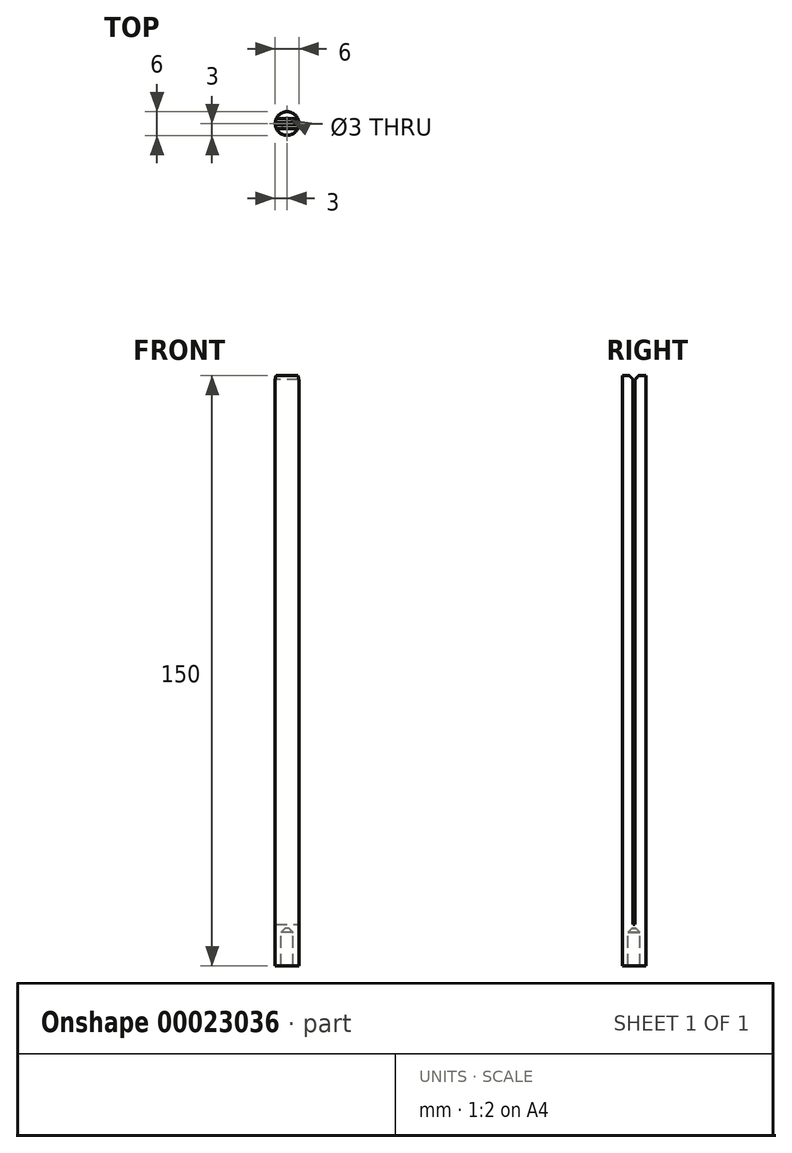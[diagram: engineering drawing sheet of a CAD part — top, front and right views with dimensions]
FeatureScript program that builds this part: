
annotation { "Feature Type Name" : "Feature", "Feature Type Description" : "" }
export const myFeature = defineFeature(function(context is Context, id is Id, definition is map)
    precondition{}
    {
        {
            var Q0;
            Q0=qCreatedBy(makeId("Top.planeOp"),FACE);
            var sketch = newSketch(context, id + "F0", { "sketchPlane" : qUnion([Q0])});
            skCircle(sketch, "E0", {"center": v(0, 0) * mm, "radius": 1.5 * mm});
            skCircle(sketch, "E1", {"center": v(0, 0) * mm, "radius": 3 * mm});
            skLineSegment(sketch, "E2", {"start": v(-3, 0) * mm, "end": v(3, 0) * mm, "construction": true});
            skLineSegment(sketch, "E3", {"start": v(-2.99, 0.25) * mm, "end": v(2.99, 0.25) * mm});
            skLineSegment(sketch, "E4.MirrorCS", {"start": v(-2.99, -0.25) * mm, "end": v(2.99, -0.25) * mm});
            skSolve(sketch);
        }
        {
            var Q0;
            {var subQ0=sQuery(id+"F0.wireOp",EDGE,"E3");var subQ1=sQuery(id+"F0.wireOp",EDGE,"E0");var subQ5=makeQuery(id+"F0.imprint","INTERSECT",VERTEX,{"disambiguationData":[OD(0.0)],"derivedFrom":[subQ1,subQ0]});Q0=makeQuery(id+"F0.imprint","IMPRINT",FACE,{"disambiguationData":[TD([[makeQuery(id+"F0.imprint","IMPRINT",EDGE,{"disambiguationData":[TD([[subQ5,1.0]])],"derivedFrom":subQ1}),-1.0]])]});}
            var Q1;
            {var subQ0=sQuery(id+"F0.wireOp",EDGE,"E3");var subQ1=sQuery(id+"F0.wireOp",EDGE,"E0");var subQ3=makeQuery(id+"F0.imprint","INTERSECT",VERTEX,{"disambiguationData":[OD(0.0)],"derivedFrom":[subQ1,subQ0]});Q1=makeQuery(id+"F0.imprint","IMPRINT",FACE,{"disambiguationData":[TD([[makeQuery(id+"F0.imprint","IMPRINT",EDGE,{"disambiguationData":[TD([[subQ3,1.0]])],"derivedFrom":subQ1}),1.0]])]});}
            var Q2;
            {var subQ0=sQuery(id+"F0.wireOp",EDGE,"E4.MirrorCS");var subQ1=sQuery(id+"F0.wireOp",EDGE,"E0");var subQ5=makeQuery(id+"F0.imprint","INTERSECT",VERTEX,{"disambiguationData":[OD(0.0)],"derivedFrom":[subQ1,subQ0]});Q2=makeQuery(id+"F0.imprint","IMPRINT",FACE,{"disambiguationData":[TD([[makeQuery(id+"F0.imprint","IMPRINT",EDGE,{"disambiguationData":[TD([[subQ5,-1.0]])],"derivedFrom":subQ1}),-1.0]])]});}
            var Q3;
            {var subQ0=sQuery(id+"F0.wireOp",EDGE,"E4.MirrorCS");var subQ1=sQuery(id+"F0.wireOp",EDGE,"E0");var subQ3=makeQuery(id+"F0.imprint","INTERSECT",VERTEX,{"disambiguationData":[OD(0.0)],"derivedFrom":[subQ1,subQ0]});Q3=makeQuery(id+"F0.imprint","IMPRINT",FACE,{"disambiguationData":[TD([[makeQuery(id+"F0.imprint","IMPRINT",EDGE,{"disambiguationData":[TD([[subQ3,-1.0]])],"derivedFrom":subQ1}),1.0]])]});}
            extrude(context, id + "F1", {"entities" : qUnion([Q0, Q1, Q2, Q3]), "depth" : 140 * mm});
        }
        {
            var Q0;
            {var subQ0=sQuery(id+"F0.wireOp",EDGE,"E4.MirrorCS");var subQ1=sQuery(id+"F0.wireOp",EDGE,"E0");var subQ3=makeQuery(id+"F0.imprint","INTERSECT",VERTEX,{"disambiguationData":[OD(0.0)],"derivedFrom":[subQ1,subQ0]});Q0=makeQuery(id+"F0.imprint","IMPRINT",FACE,{"disambiguationData":[TD([[makeQuery(id+"F0.imprint","IMPRINT",EDGE,{"disambiguationData":[TD([[subQ3,-1.0]])],"derivedFrom":subQ1}),1.0]])]});}
            var Q1;
            {var subQ0=sQuery(id+"F0.wireOp",EDGE,"E3");var subQ1=sQuery(id+"F0.wireOp",EDGE,"E0");var subQ3=makeQuery(id+"F0.imprint","INTERSECT",VERTEX,{"disambiguationData":[OD(0.0)],"derivedFrom":[subQ1,subQ0]});Q1=makeQuery(id+"F0.imprint","IMPRINT",FACE,{"disambiguationData":[TD([[makeQuery(id+"F0.imprint","IMPRINT",EDGE,{"disambiguationData":[TD([[subQ3,-1.0]])],"derivedFrom":subQ1}),1.0]])]});}
            var Q2;
            {var subQ0=sQuery(id+"F0.wireOp",EDGE,"E3");var subQ1=sQuery(id+"F0.wireOp",EDGE,"E0");var subQ3=makeQuery(id+"F0.imprint","INTERSECT",VERTEX,{"disambiguationData":[OD(0.0)],"derivedFrom":[subQ1,subQ0]});Q2=makeQuery(id+"F0.imprint","IMPRINT",FACE,{"disambiguationData":[TD([[makeQuery(id+"F0.imprint","IMPRINT",EDGE,{"disambiguationData":[TD([[subQ3,1.0]])],"derivedFrom":subQ1}),1.0]])]});}
            var Q3;
            {var subQ0=sQuery(id+"F0.wireOp",EDGE,"E4.MirrorCS");var subQ1=sQuery(id+"F0.wireOp",EDGE,"E0");var subQ5=makeQuery(id+"F0.imprint","INTERSECT",VERTEX,{"disambiguationData":[OD(0.0)],"derivedFrom":[subQ1,subQ0]});Q3=makeQuery(id+"F0.imprint","IMPRINT",FACE,{"disambiguationData":[TD([[makeQuery(id+"F0.imprint","IMPRINT",EDGE,{"disambiguationData":[TD([[subQ5,-1.0]])],"derivedFrom":subQ1}),-1.0]])]});}
            var Q4;
            {var subQ0=sQuery(id+"F0.wireOp",EDGE,"E3");var subQ1=sQuery(id+"F0.wireOp",EDGE,"E0");var subQ5=makeQuery(id+"F0.imprint","INTERSECT",VERTEX,{"disambiguationData":[OD(0.0)],"derivedFrom":[subQ1,subQ0]});Q4=makeQuery(id+"F0.imprint","IMPRINT",FACE,{"disambiguationData":[TD([[makeQuery(id+"F0.imprint","IMPRINT",EDGE,{"disambiguationData":[TD([[subQ5,1.0]])],"derivedFrom":subQ1}),-1.0]])]});}
            var Q5;
            {var subQ1=sQuery(id+"F0.wireOp",EDGE,"E0");var subQ5=sQuery(id+"F0.wireOp",EDGE,"E3");var subQ6=makeQuery(id+"F0.imprint","INTERSECT",VERTEX,{"disambiguationData":[OD(1.0)],"derivedFrom":[subQ1,subQ5]});Q5=makeQuery(id+"F0.imprint","IMPRINT",FACE,{"disambiguationData":[TD([[makeQuery(id+"F0.imprint","IMPRINT",EDGE,{"disambiguationData":[TD([[subQ6,1.0]])],"derivedFrom":subQ1}),-1.0]])]});}
            var Q6;
            {var subQ1=sQuery(id+"F0.wireOp",EDGE,"E0");var subQ5=sQuery(id+"F0.wireOp",EDGE,"E3");var subQ6=makeQuery(id+"F0.imprint","INTERSECT",VERTEX,{"disambiguationData":[OD(0.0)],"derivedFrom":[subQ1,subQ5]});Q6=makeQuery(id+"F0.imprint","IMPRINT",FACE,{"disambiguationData":[TD([[makeQuery(id+"F0.imprint","IMPRINT",EDGE,{"disambiguationData":[TD([[subQ6,-1.0]])],"derivedFrom":subQ1}),-1.0]])]});}
            extrude(context, id + "F2", {"entities" : qUnion([Q0, Q1, Q2, Q3, Q4, Q5, Q6]), "operationType" : NewBodyOperationType.ADD, "endBound" : BoundingType.SYMMETRIC, "depth" : 1 * mm});
        }
        {
            var Q0;
            Q0=makeQuery(id+"F0.imprint","IMPRINT",FACE,{"disambiguationData":[TD([[makeQuery(id+"F0.imprint","IMPRINT",EDGE,{"derivedFrom":sQuery(id+"F0.wireOp",EDGE,"E1")}),1.0]])]});
            extrude(context, id + "F3", {"entities" : qUnion([Q0]), "operationType" : NewBodyOperationType.ADD, "oppositeDirection" : true, "depth" : 10 * mm});
        }
        {
            var Q0;
            Q0=makeQuery(id+"F3.boolean.opBoolean","INTERSECT",EDGE,{"derivedFrom":[makeQuery(id+"F2.opExtrude","CAP_FACE",FACE,{"disambiguationData":[OSD([sQuery(id+"F0.wireOp",EDGE,"E1")])],"isStart":true}),makeQuery(id+"F3.opExtrude","SWEPT_FACE",FACE,{"disambiguationData":[OSD([sQuery(id+"F0.wireOp",EDGE,"E0")])]})]});
            chamfer(context, id + "F4", {"entities" : qUnion([Q0]), "width" : 1 * mm, "tangentPropagation" : true});
        }
        {
            var Q0;
            Q0=makeQuery(id+"F1.opExtrude","CAP_EDGE",EDGE,{"disambiguationData":[OSD([sQuery(id+"F0.wireOp",EDGE,"E3")])],"isStart":false});
            var Q1;
            Q1=makeQuery(id+"F1.opExtrude","CAP_EDGE",EDGE,{"disambiguationData":[OSD([sQuery(id+"F0.wireOp",EDGE,"E4.MirrorCS")])],"isStart":false});
            chamfer(context, id + "F5", {"entities" : qUnion([Q0, Q1]), "width" : 1 * mm, "tangentPropagation" : true});
        }
    });
